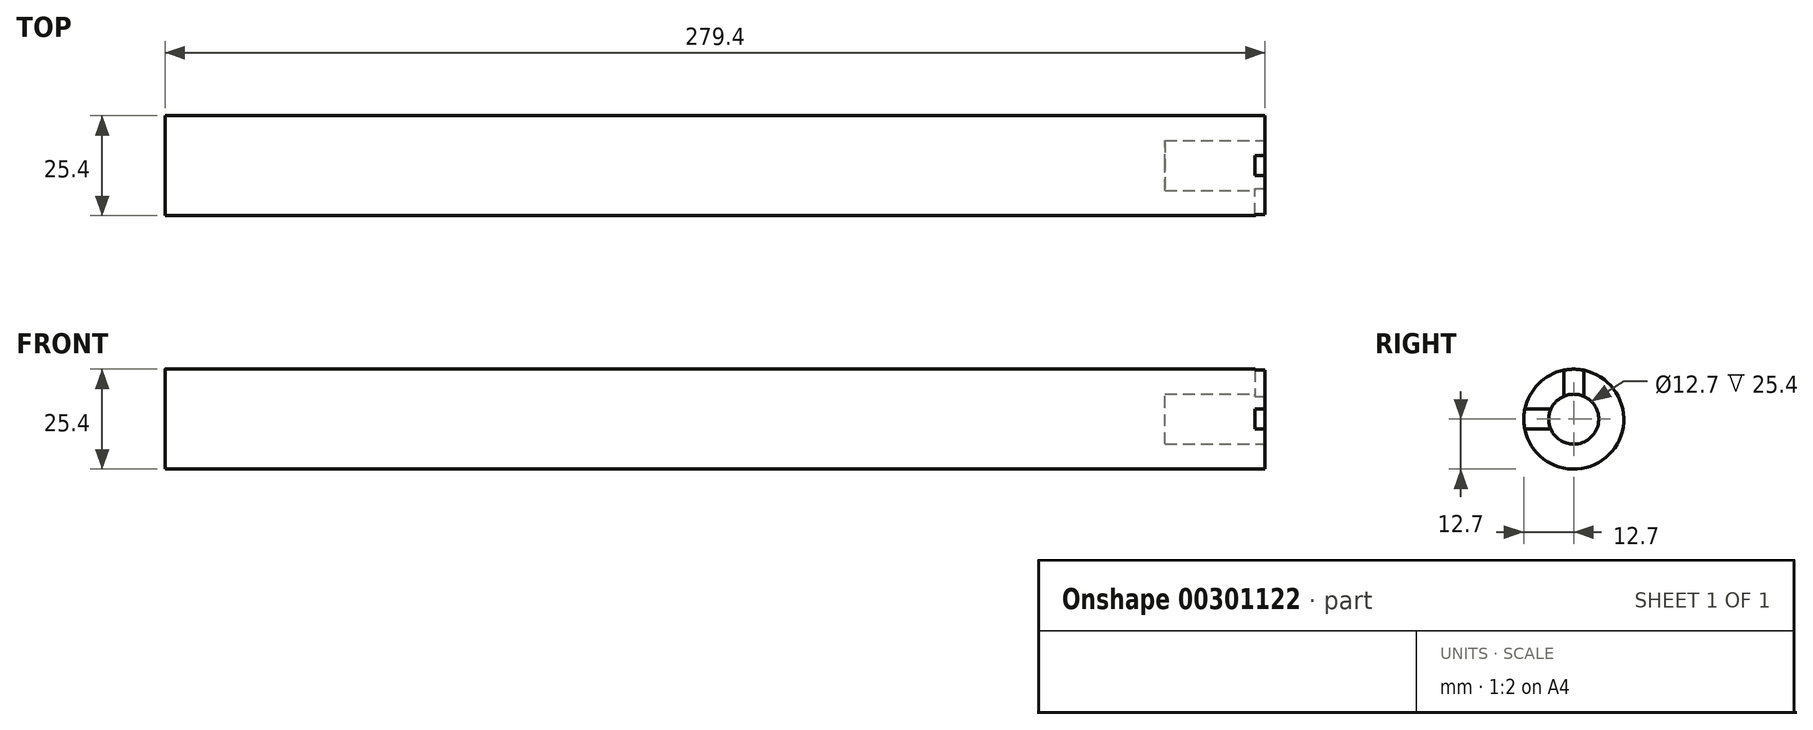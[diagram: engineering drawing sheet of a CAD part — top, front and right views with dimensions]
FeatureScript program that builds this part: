
annotation { "Feature Type Name" : "Feature", "Feature Type Description" : "" }
export const myFeature = defineFeature(function(context is Context, id is Id, definition is map)
    precondition{}
    {
        {
            var Q0;
            Q0=qCreatedBy(makeId("Right.planeOp"),FACE);
            var sketch = newSketch(context, id + "F0", { "sketchPlane" : qUnion([Q0])});
            skCircle(sketch, "E0", {"center": v(0, 0) * mm, "radius": 12.7 * mm});
            skSolve(sketch);
        }
        {
            var Q0;
            Q0 = qSketchRegion(id + "F0", true);
            extrude(context, id + "F1", {"entities" : qUnion([Q0]), "depth" : 279.4 * mm});
        }
        {
            var Q0;
            Q0=makeQuery(id+"F1.opExtrude","CAP_FACE",FACE,{"disambiguationData":[OSD([sQuery(id+"F0.wireOp",EDGE,"E0")])],"isStart":false});
            var sketch = newSketch(context, id + "F2", { "sketchPlane" : qUnion([Q0])});
            skCircle(sketch, "E1", {"center": v(0, 0) * mm, "radius": 6.35 * mm});
            skSolve(sketch);
        }
        {
            var Q0;
            Q0 = qSketchRegion(id + "F2", true);
            extrude(context, id + "F3", {"entities" : qUnion([Q0]), "operationType" : NewBodyOperationType.REMOVE, "oppositeDirection" : true, "depth" : 25.4 * mm});
        }
        {
            var Q0;
            Q0=makeQuery(id+"F1.opExtrude","CAP_FACE",FACE,{"disambiguationData":[OSD([sQuery(id+"F0.wireOp",EDGE,"E0")])],"isStart":false});
            var sketch = newSketch(context, id + "F4", { "sketchPlane" : qUnion([Q0])});
            skLineSegment(sketch, "E2", {"start": v(-14.16, 0) * mm, "end": v(15.3, 0) * mm});
            skLineSegment(sketch, "E3", {"start": v(0, 15.99) * mm, "end": v(0, -14.22) * mm});
            skLineSegment(sketch, "E4.bottom", {"start": v(-2.54, 15.99) * mm, "end": v(2.54, 15.99) * mm});
            skLineSegment(sketch, "E4.top", {"start": v(-2.54, -14.22) * mm, "end": v(2.54, -14.22) * mm});
            skLineSegment(sketch, "E4.left", {"start": v(-2.54, 15.99) * mm, "end": v(-2.54, -14.22) * mm});
            skLineSegment(sketch, "E4.right", {"start": v(2.54, 15.99) * mm, "end": v(2.54, -14.22) * mm});
            skLineSegment(sketch, "E5.bottom", {"start": v(-14.16, -2.54) * mm, "end": v(15.3, -2.54) * mm});
            skLineSegment(sketch, "E5.top", {"start": v(-14.16, 2.54) * mm, "end": v(15.3, 2.54) * mm});
            skLineSegment(sketch, "E5.left", {"start": v(-14.16, -2.54) * mm, "end": v(-14.16, 2.54) * mm});
            skLineSegment(sketch, "E5.right", {"start": v(15.3, -2.54) * mm, "end": v(15.3, 2.54) * mm});
            skSolve(sketch);
        }
        {
            var Q0;
            {var subQ0=sQuery(id+"F4.wireOp",EDGE,"E2");var subQ1=makeQuery(id+"F1.opExtrude","CAP_EDGE",EDGE,{"disambiguationData":[OSD([sQuery(id+"F0.wireOp",EDGE,"E0")])],"isStart":false});var subQ2=makeQuery(id+"F4.imprint","INTERSECT",VERTEX,{"disambiguationData":[OD(0.0)],"derivedFrom":[subQ1,subQ0]});Q0=makeQuery(id+"F4.imprint","IMPRINT",FACE,{"disambiguationData":[TD([[makeQuery(id+"F4.imprint","IMPRINT",EDGE,{"disambiguationData":[TD([[subQ2,-1.0]])],"derivedFrom":subQ0}),1.0]])]});}
            var Q1;
            {var subQ0=sQuery(id+"F4.wireOp",EDGE,"E3");var subQ1=makeQuery(id+"F1.opExtrude","CAP_EDGE",EDGE,{"disambiguationData":[OSD([sQuery(id+"F0.wireOp",EDGE,"E0")])],"isStart":false});var subQ2=makeQuery(id+"F4.imprint","INTERSECT",VERTEX,{"disambiguationData":[OD(0.0)],"derivedFrom":[subQ1,subQ0]});Q1=makeQuery(id+"F4.imprint","IMPRINT",FACE,{"disambiguationData":[TD([[makeQuery(id+"F4.imprint","IMPRINT",EDGE,{"disambiguationData":[TD([[subQ2,-1.0]])],"derivedFrom":subQ0}),-1.0]])]});}
            var Q2;
            {var subQ0=sQuery(id+"F4.wireOp",EDGE,"E3");var subQ1=makeQuery(id+"F1.opExtrude","CAP_EDGE",EDGE,{"disambiguationData":[OSD([sQuery(id+"F0.wireOp",EDGE,"E0")])],"isStart":false});var subQ2=makeQuery(id+"F4.imprint","INTERSECT",VERTEX,{"disambiguationData":[OD(0.0)],"derivedFrom":[subQ1,subQ0]});Q2=makeQuery(id+"F4.imprint","IMPRINT",FACE,{"disambiguationData":[TD([[makeQuery(id+"F4.imprint","IMPRINT",EDGE,{"disambiguationData":[TD([[subQ2,-1.0]])],"derivedFrom":subQ0}),1.0]])]});}
            var Q3;
            {var subQ0=sQuery(id+"F4.wireOp",EDGE,"E2");var subQ1=makeQuery(id+"F3.boolean.opBoolean","COPY",EDGE,{"derivedFrom":makeQuery(id+"F3.opExtrude","CAP_EDGE",EDGE,{"disambiguationData":[OSD([sQuery(id+"F2.wireOp",EDGE,"E1")])],"isStart":true})});var subQ2=makeQuery(id+"F4.imprint","INTERSECT",VERTEX,{"disambiguationData":[OD(1.0)],"derivedFrom":[subQ1,subQ0]});Q3=makeQuery(id+"F4.imprint","IMPRINT",FACE,{"disambiguationData":[TD([[makeQuery(id+"F4.imprint","IMPRINT",EDGE,{"disambiguationData":[TD([[subQ2,-1.0]])],"derivedFrom":subQ0}),1.0]])]});}
            var Q4;
            {var subQ0=sQuery(id+"F4.wireOp",EDGE,"E2");var subQ1=makeQuery(id+"F3.boolean.opBoolean","COPY",EDGE,{"derivedFrom":makeQuery(id+"F3.opExtrude","CAP_EDGE",EDGE,{"disambiguationData":[OSD([sQuery(id+"F2.wireOp",EDGE,"E1")])],"isStart":true})});var subQ2=makeQuery(id+"F4.imprint","INTERSECT",VERTEX,{"disambiguationData":[OD(1.0)],"derivedFrom":[subQ1,subQ0]});Q4=makeQuery(id+"F4.imprint","IMPRINT",FACE,{"disambiguationData":[TD([[makeQuery(id+"F4.imprint","IMPRINT",EDGE,{"disambiguationData":[TD([[subQ2,-1.0]])],"derivedFrom":subQ0}),-1.0]])]});}
            var Q5;
            {var subQ0=sQuery(id+"F4.wireOp",EDGE,"E2");var subQ1=makeQuery(id+"F1.opExtrude","CAP_EDGE",EDGE,{"disambiguationData":[OSD([sQuery(id+"F0.wireOp",EDGE,"E0")])],"isStart":false});var subQ2=makeQuery(id+"F4.imprint","INTERSECT",VERTEX,{"disambiguationData":[OD(0.0)],"derivedFrom":[subQ1,subQ0]});Q5=makeQuery(id+"F4.imprint","IMPRINT",FACE,{"disambiguationData":[TD([[makeQuery(id+"F4.imprint","IMPRINT",EDGE,{"disambiguationData":[TD([[subQ2,-1.0]])],"derivedFrom":subQ0}),-1.0]])]});}
            var Q6;
            {var subQ0=sQuery(id+"F4.wireOp",EDGE,"E3");var subQ1=makeQuery(id+"F3.boolean.opBoolean","COPY",EDGE,{"derivedFrom":makeQuery(id+"F3.opExtrude","CAP_EDGE",EDGE,{"disambiguationData":[OSD([sQuery(id+"F2.wireOp",EDGE,"E1")])],"isStart":true})});var subQ2=makeQuery(id+"F4.imprint","INTERSECT",VERTEX,{"disambiguationData":[OD(1.0)],"derivedFrom":[subQ1,subQ0]});Q6=makeQuery(id+"F4.imprint","IMPRINT",FACE,{"disambiguationData":[TD([[makeQuery(id+"F4.imprint","IMPRINT",EDGE,{"disambiguationData":[TD([[subQ2,-1.0]])],"derivedFrom":subQ0}),-1.0]])]});}
            var Q7;
            {var subQ0=sQuery(id+"F4.wireOp",EDGE,"E3");var subQ1=makeQuery(id+"F3.boolean.opBoolean","COPY",EDGE,{"derivedFrom":makeQuery(id+"F3.opExtrude","CAP_EDGE",EDGE,{"disambiguationData":[OSD([sQuery(id+"F2.wireOp",EDGE,"E1")])],"isStart":true})});var subQ2=makeQuery(id+"F4.imprint","INTERSECT",VERTEX,{"disambiguationData":[OD(1.0)],"derivedFrom":[subQ1,subQ0]});Q7=makeQuery(id+"F4.imprint","IMPRINT",FACE,{"disambiguationData":[TD([[makeQuery(id+"F4.imprint","IMPRINT",EDGE,{"disambiguationData":[TD([[subQ2,-1.0]])],"derivedFrom":subQ0}),1.0]])]});}
            extrude(context, id + "F5", {"entities" : qUnion([Q0, Q1, Q2, Q3, Q4, Q5, Q6, Q7]), "operationType" : NewBodyOperationType.REMOVE, "oppositeDirection" : true, "depth" : 2.54 * mm});
        }
    });
